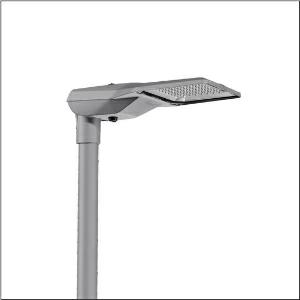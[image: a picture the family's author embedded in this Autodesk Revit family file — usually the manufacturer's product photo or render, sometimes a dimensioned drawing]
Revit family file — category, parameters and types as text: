
# Revit family: streetlight_sl_21_iq_midi___pc-r_5xe3g31y08mb_65a2
name_source: partatom
category: Lighting Fixtures
units: mm (PartAtom-declared; Revit-internal decimal feet)

## family parameters
Cut with Voids When Loaded = No
Host = Face
Light Source = No
Part Type = Normal
Room Calculation Point = No
Round Connector Dimension = Use Diameter
Shared = No

## types (1)
- --- (1 x LED, 17070 lm, 129.3 W, 3000K)
    Apparent Load = 129 VA
    CIE Flux Codes = 38 78 98 100 100
    Color Rendering = 70
    Color Temperature = 3000K
    Default Elevation = 1800 mm
    Description = Streetlight SL 21 iQ midi, mast luminaire, primary light control with lens, of PMMA, primary optical cover: cover, of toughened safety glass, transparent, light distribution: PC-R, light emission: direct distribution, primary light characteristic: asymmetric, right, installation type: post-top, side-entry, LED, High Power LED, rated luminous flux: 17.070lm, luminous efficacy: 132lm/W, light colour: 730, colour temperature: 3000K, control: presetting dimming logarithmic, Street-Remote, Auto-Match, Temp-Guard, Lumen-Switch, Night-Set, Smart-Wire, Light-Fading, Desk-Remote (wireless, voltage-free reading and setting of iQ features in the workshop via application-optimized NFC function/RFID function), optimised constant luminous flux control (CLO 2.0), mains connection: 230..240V, AC, 50/60Hz, start of lifetime: 129W, end of service life: 142W, reduction: 56W, luminaire housing, of diecast aluminium, powder-coated, Siteco® metallic grey (DB 702S), corrosivity category C5 mid according to DIN EN ISO 12944, please order mast flange separately, inclination adjustable: 0°, 5°, 10°, 15°, sealing non-destructively replaceable, multi-level sealing system, length: 644mm, width: 335mm, height: 110mm, mast flange for spigot size: 42mm (side-entry): 5XC10008XM4, 60/48mm (side-entry/post-top): 5XC10108XM2, 76/60mm (side-entry/post-top): 5XC10108XM1, Smart Interface below and above, protection rating (complete): IP66, insulation class (complete): insulation class II (safety insulation), certification: CE, ENEC, ENEC+, VDE, impact resistance: IK09, permissible operating ambient temperature for outdoor applications: -40..+50°C, standard-compliant lighting for roads and squares, packaging unit: 1 piece

Light Distribution: PC-R
    Height = 111 mm
    Lamp = 1 x LED
    Lamp Light Flux = 17070 lm
    Lamp Power = 129.3 W
    Lamp count = 1
    Length = 644 mm
    Luminous efficacy = 132 lm/W
    Manufacturer = Siteco
    ModVariant = No
    Model = 5XE3G31Y08MB
    Number of Poles = 1
    OnlyDefault = Yes
    Power Factor = 1
    Product Name = Streetlight SL 21 iQ midi | PC-R
    Product group = mast luminaire | pylon top
    ProductGroupID = 6100
    Protection Class = Protection class II
    Protection Degree = IP 66
    RLX_Detail_Level = 1
    RLX_Emergency_Light_Flux = 0 lm
    RLX_Emergency_Type = 0
    RLX_Emergency_Type_DB = No
    RlxData = <blob elided: 93569 chars, md5=de239867>
    Socket = socket
    Standby Power = 0 W
    System Light Flux = 17070 lm
    System Power = 129 W
    Type Comments = factory setting: luminous flux: 100 % | dim-lin: 254 | 672 mA
    Type Image = l_1004304.jpg
    URL = http://relux.com
    VarID = @adj_005295
    Voltage = 0 V
    Weight = 0.00 kg
    Width = 336 mm

## geometry (parser evidence)
native form markers: Blend x4, Sweep x10
no freeform markers — native parametric forms only
